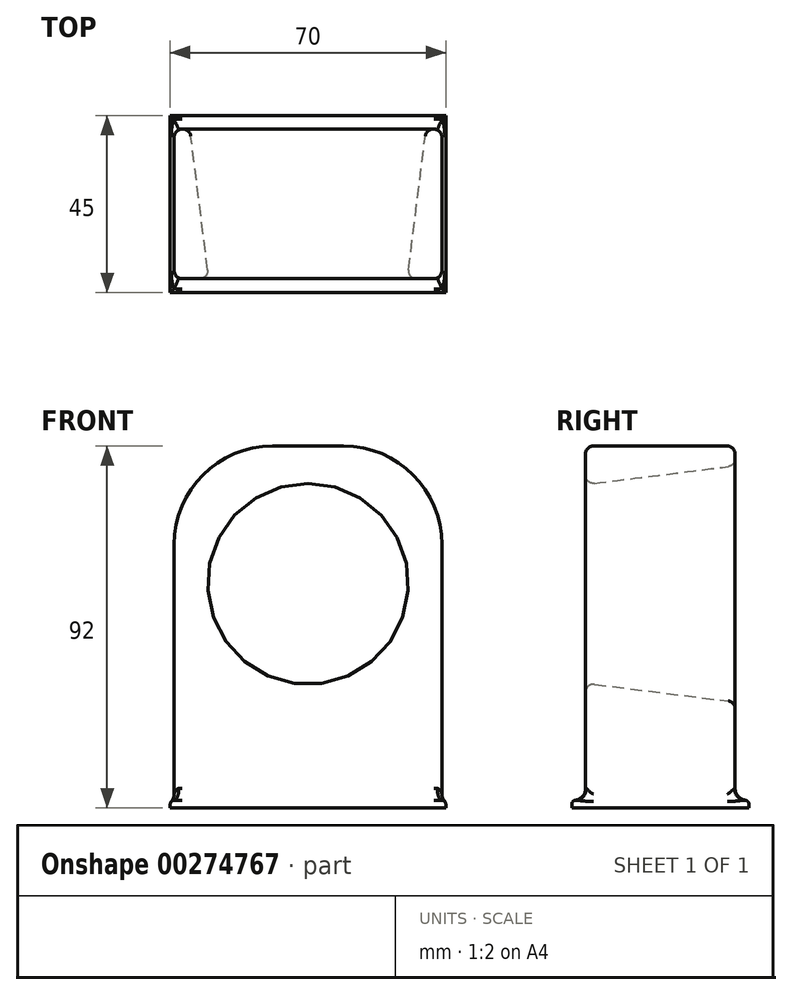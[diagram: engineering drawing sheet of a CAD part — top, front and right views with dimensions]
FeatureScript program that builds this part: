
annotation { "Feature Type Name" : "Feature", "Feature Type Description" : "" }
export const myFeature = defineFeature(function(context is Context, id is Id, definition is map)
    precondition{}
    {
        {
            var Q0;
            Q0=qCreatedBy(makeId("Top.planeOp"),FACE);
            var sketch = newSketch(context, id + "F0", { "sketchPlane" : qUnion([Q0])});
            skLineSegment(sketch, "E0.bottom", {"start": v(-35, 22.5) * mm, "end": v(35, 22.5) * mm});
            skLineSegment(sketch, "E0.top", {"start": v(-35, -22.5) * mm, "end": v(35, -22.5) * mm});
            skLineSegment(sketch, "E0.left", {"start": v(-35, 22.5) * mm, "end": v(-35, -22.5) * mm});
            skLineSegment(sketch, "E0.right", {"start": v(35, 22.5) * mm, "end": v(35, -22.5) * mm});
            skSolve(sketch);
        }
        {
            var Q0;
            Q0 = qSketchRegion(id + "F0", true);
            extrude(context, id + "F1", {"entities" : qUnion([Q0]), "depth" : 2 * mm});
        }
        {
            var Q0;
            Q0=makeQuery(id+"F1.opExtrude","CAP_EDGE",EDGE,{"disambiguationData":[OSD([sQuery(id+"F0.wireOp",EDGE,"E0.top")])],"isStart":false});
            var Q1;
            Q1=makeQuery(id+"F1.opExtrude","CAP_EDGE",EDGE,{"disambiguationData":[OSD([sQuery(id+"F0.wireOp",EDGE,"E0.right")])],"isStart":false});
            var Q2;
            Q2=makeQuery(id+"F1.opExtrude","CAP_EDGE",EDGE,{"disambiguationData":[OSD([sQuery(id+"F0.wireOp",EDGE,"E0.left")])],"isStart":false});
            var Q3;
            Q3=makeQuery(id+"F1.opExtrude","CAP_EDGE",EDGE,{"disambiguationData":[OSD([sQuery(id+"F0.wireOp",EDGE,"E0.bottom")])],"isStart":false});
            fillet(context, id + "F8", {"entities" : qUnion([Q0, Q1, Q2, Q3]), "radius" : 1 * mm, "tangentPropagation" : true, "allowEdgeOverflow" : false});
        }
        {
            var Q0;
            Q0=makeQuery(id+"F1.opExtrude","CAP_FACE",FACE,{"disambiguationData":[OSD([sQuery(id+"F0.wireOp",EDGE,"E0.bottom"),sQuery(id+"F0.wireOp",EDGE,"E0.top"),sQuery(id+"F0.wireOp",EDGE,"E0.left"),sQuery(id+"F0.wireOp",EDGE,"E0.right")])],"isStart":false});
            var sketch = newSketch(context, id + "F2", { "sketchPlane" : qUnion([Q0])});
            skLineSegment(sketch, "E1.bottom", {"start": v(-34, 19) * mm, "end": v(34, 19) * mm});
            skLineSegment(sketch, "E1.top", {"start": v(-34, -19) * mm, "end": v(34, -19) * mm});
            skLineSegment(sketch, "E1.left", {"start": v(-34, 19) * mm, "end": v(-34, -19) * mm});
            skLineSegment(sketch, "E1.right", {"start": v(34, 19) * mm, "end": v(34, -19) * mm});
            skSolve(sketch);
        }
        {
            var Q0;
            Q0 = qSketchRegion(id + "F2", true);
            extrude(context, id + "F9", {"entities" : qUnion([Q0]), "operationType" : NewBodyOperationType.ADD, "depth" : 90 * mm});
        }
        {
            var Q0;
            Q0=makeQuery(id+"F9.opExtrude","CAP_EDGE",EDGE,{"disambiguationData":[OSD([sQuery(id+"F2.wireOp",EDGE,"E1.right")])],"isStart":false});
            var Q1;
            Q1=makeQuery(id+"F9.opExtrude","CAP_EDGE",EDGE,{"disambiguationData":[OSD([sQuery(id+"F2.wireOp",EDGE,"E1.left")])],"isStart":false});
            fillet(context, id + "F3", {"entities" : qUnion([Q0, Q1]), "radius" : 25 * mm, "tangentPropagation" : true, "allowEdgeOverflow" : false});
        }
        {
            var Q0;
            Q0=makeQuery(id+"F9.opExtrude","SWEPT_FACE",FACE,{"disambiguationData":[OSD([sQuery(id+"F2.wireOp",EDGE,"E1.top")])]});
            var sketch = newSketch(context, id + "F10", { "sketchPlane" : qUnion([Q0])});
            skCircle(sketch, "E2", {"center": v(0, 57) * mm, "radius": 25 * mm});
            skSolve(sketch);
        }
        {
            var Q0;
            Q0 = qSketchRegion(id + "F10", true);
            extrude(context, id + "F4", {"entities" : qUnion([Q0]), "operationType" : NewBodyOperationType.REMOVE, "oppositeDirection" : true, "depth" : 50 * mm});
        }
        {
            var Q0;
            Q0=makeQuery(id+"F4.boolean.opBoolean","INTERSECT",EDGE,{"derivedFrom":[makeQuery(id+"F9.opExtrude","SWEPT_FACE",FACE,{"disambiguationData":[OSD([sQuery(id+"F2.wireOp",EDGE,"E1.bottom")])]}),makeQuery(id+"F4.opExtrude","SWEPT_FACE",FACE,{"disambiguationData":[OSD([sQuery(id+"F10.wireOp",EDGE,"E2")])]})]});
            chamfer(context, id + "F5", {"entities" : qUnion([Q0]), "chamferType" : ChamferType.TWO_OFFSETS, "width1" : 40 * mm, "oppositeDirection" : false, "width2" : 5 * mm, "tangentPropagation" : true});
        }
        {
            var Q0;
            Q0=makeQuery(id+"F5.opChamfer","BLEND_EDGE",EDGE,{"blendedFrom":[makeQuery(id+"F4.boolean.opBoolean","INTERSECT",EDGE,{"derivedFrom":[makeQuery(id+"F9.opExtrude","SWEPT_FACE",FACE,{"disambiguationData":[OSD([sQuery(id+"F2.wireOp",EDGE,"E1.bottom")])]}),makeQuery(id+"F4.opExtrude","SWEPT_FACE",FACE,{"disambiguationData":[OSD([sQuery(id+"F10.wireOp",EDGE,"E2")])]})]}),makeQuery(id+"F9.opExtrude","SWEPT_FACE",FACE,{"disambiguationData":[OSD([sQuery(id+"F2.wireOp",EDGE,"E1.top")])]})],"blendedInto":[makeQuery(id+"F9.opExtrude","SWEPT_FACE",FACE,{"disambiguationData":[OSD([sQuery(id+"F2.wireOp",EDGE,"E1.top")])]})]});
            var Q1;
            {var subQ0=makeQuery(id+"F9.opExtrude","SWEPT_FACE",FACE,{"disambiguationData":[OSD([sQuery(id+"F2.wireOp",EDGE,"E1.bottom")])]});Q1=makeQuery(id+"F5.opChamfer","BLEND_EDGE",EDGE,{"blendedFrom":[makeQuery(id+"F4.boolean.opBoolean","INTERSECT",EDGE,{"derivedFrom":[subQ0,makeQuery(id+"F4.opExtrude","SWEPT_FACE",FACE,{"disambiguationData":[OSD([sQuery(id+"F10.wireOp",EDGE,"E2")])]})]}),subQ0],"blendedInto":[subQ0]});}
            var Q2;
            Q2=makeQuery(id+"F3.opFillet","BLEND_EDGE",EDGE,{"blendedFrom":[makeQuery(id+"F9.opExtrude","CAP_EDGE",EDGE,{"disambiguationData":[OSD([sQuery(id+"F2.wireOp",EDGE,"E1.left")])],"isStart":false}),makeQuery(id+"F9.opExtrude","SWEPT_FACE",FACE,{"disambiguationData":[OSD([sQuery(id+"F2.wireOp",EDGE,"E1.bottom")])]})],"blendedInto":[makeQuery(id+"F9.opExtrude","SWEPT_FACE",FACE,{"disambiguationData":[OSD([sQuery(id+"F2.wireOp",EDGE,"E1.bottom")])]})]});
            var Q3;
            Q3=makeQuery(id+"F9.opExtrude","CAP_EDGE",EDGE,{"disambiguationData":[OSD([sQuery(id+"F2.wireOp",EDGE,"E1.bottom")])],"isStart":false});
            var Q4;
            Q4=makeQuery(id+"F3.opFillet","BLEND_EDGE",EDGE,{"blendedFrom":[makeQuery(id+"F9.opExtrude","CAP_EDGE",EDGE,{"disambiguationData":[OSD([sQuery(id+"F2.wireOp",EDGE,"E1.right")])],"isStart":false}),makeQuery(id+"F9.opExtrude","SWEPT_FACE",FACE,{"disambiguationData":[OSD([sQuery(id+"F2.wireOp",EDGE,"E1.bottom")])]})],"blendedInto":[makeQuery(id+"F9.opExtrude","SWEPT_FACE",FACE,{"disambiguationData":[OSD([sQuery(id+"F2.wireOp",EDGE,"E1.bottom")])]})]});
            var Q5;
            Q5=makeQuery(id+"F9.opExtrude","SWEPT_EDGE",EDGE,{"disambiguationData":[OSD([sQuery(id+"F0.wireOp",EDGE,"E0.bottom"),sQuery(id+"F0.wireOp",EDGE,"E0.top"),sQuery(id+"F0.wireOp",EDGE,"E0.left"),sQuery(id+"F0.wireOp",EDGE,"E0.right"),sQuery(id+"F2.wireOp",EDGE,"E1.bottom"),sQuery(id+"F2.wireOp",EDGE,"E1.right")])]});
            var Q6;
            Q6=makeQuery(id+"F9.opExtrude","SWEPT_EDGE",EDGE,{"disambiguationData":[OSD([sQuery(id+"F0.wireOp",EDGE,"E0.bottom"),sQuery(id+"F0.wireOp",EDGE,"E0.top"),sQuery(id+"F0.wireOp",EDGE,"E0.left"),sQuery(id+"F0.wireOp",EDGE,"E0.right"),sQuery(id+"F2.wireOp",EDGE,"E1.bottom"),sQuery(id+"F2.wireOp",EDGE,"E1.left")])]});
            var Q7;
            Q7=makeQuery(id+"F3.opFillet","BLEND_EDGE",EDGE,{"blendedFrom":[makeQuery(id+"F9.opExtrude","CAP_EDGE",EDGE,{"disambiguationData":[OSD([sQuery(id+"F2.wireOp",EDGE,"E1.right")])],"isStart":false}),makeQuery(id+"F9.opExtrude","SWEPT_FACE",FACE,{"disambiguationData":[OSD([sQuery(id+"F2.wireOp",EDGE,"E1.top")])]})],"blendedInto":[makeQuery(id+"F9.opExtrude","SWEPT_FACE",FACE,{"disambiguationData":[OSD([sQuery(id+"F2.wireOp",EDGE,"E1.top")])]})]});
            var Q8;
            Q8=makeQuery(id+"F9.opExtrude","CAP_EDGE",EDGE,{"disambiguationData":[OSD([sQuery(id+"F2.wireOp",EDGE,"E1.top")])],"isStart":false});
            var Q9;
            Q9=makeQuery(id+"F9.opExtrude","SWEPT_EDGE",EDGE,{"disambiguationData":[OSD([sQuery(id+"F0.wireOp",EDGE,"E0.bottom"),sQuery(id+"F0.wireOp",EDGE,"E0.top"),sQuery(id+"F0.wireOp",EDGE,"E0.left"),sQuery(id+"F0.wireOp",EDGE,"E0.right"),sQuery(id+"F2.wireOp",EDGE,"E1.top"),sQuery(id+"F2.wireOp",EDGE,"E1.right")])]});
            var Q10;
            Q10=makeQuery(id+"F9.opExtrude","SWEPT_EDGE",EDGE,{"disambiguationData":[OSD([sQuery(id+"F0.wireOp",EDGE,"E0.bottom"),sQuery(id+"F0.wireOp",EDGE,"E0.top"),sQuery(id+"F0.wireOp",EDGE,"E0.left"),sQuery(id+"F0.wireOp",EDGE,"E0.right"),sQuery(id+"F2.wireOp",EDGE,"E1.top"),sQuery(id+"F2.wireOp",EDGE,"E1.left")])]});
            var Q11;
            Q11=makeQuery(id+"F3.opFillet","BLEND_EDGE",EDGE,{"blendedFrom":[makeQuery(id+"F9.opExtrude","CAP_EDGE",EDGE,{"disambiguationData":[OSD([sQuery(id+"F2.wireOp",EDGE,"E1.left")])],"isStart":false}),makeQuery(id+"F9.opExtrude","SWEPT_FACE",FACE,{"disambiguationData":[OSD([sQuery(id+"F2.wireOp",EDGE,"E1.top")])]})],"blendedInto":[makeQuery(id+"F9.opExtrude","SWEPT_FACE",FACE,{"disambiguationData":[OSD([sQuery(id+"F2.wireOp",EDGE,"E1.top")])]})]});
            fillet(context, id + "F6", {"entities" : qUnion([Q0, Q1, Q2, Q3, Q4, Q5, Q6, Q7, Q8, Q9, Q10, Q11]), "radius" : 2 * mm, "tangentPropagation" : true, "allowEdgeOverflow" : false});
        }
        {
            var Q0;
            Q0=makeQuery(id+"F9.opExtrude","CAP_EDGE",EDGE,{"disambiguationData":[OSD([sQuery(id+"F2.wireOp",EDGE,"E1.bottom")])],"isStart":true});
            var Q1;
            Q1=makeQuery(id+"F9.opExtrude","CAP_EDGE",EDGE,{"disambiguationData":[OSD([sQuery(id+"F2.wireOp",EDGE,"E1.top")])],"isStart":true});
            fillet(context, id + "F7", {"entities" : qUnion([Q0, Q1]), "radius" : 3 * mm, "tangentPropagation" : true, "allowEdgeOverflow" : false});
        }
    });
